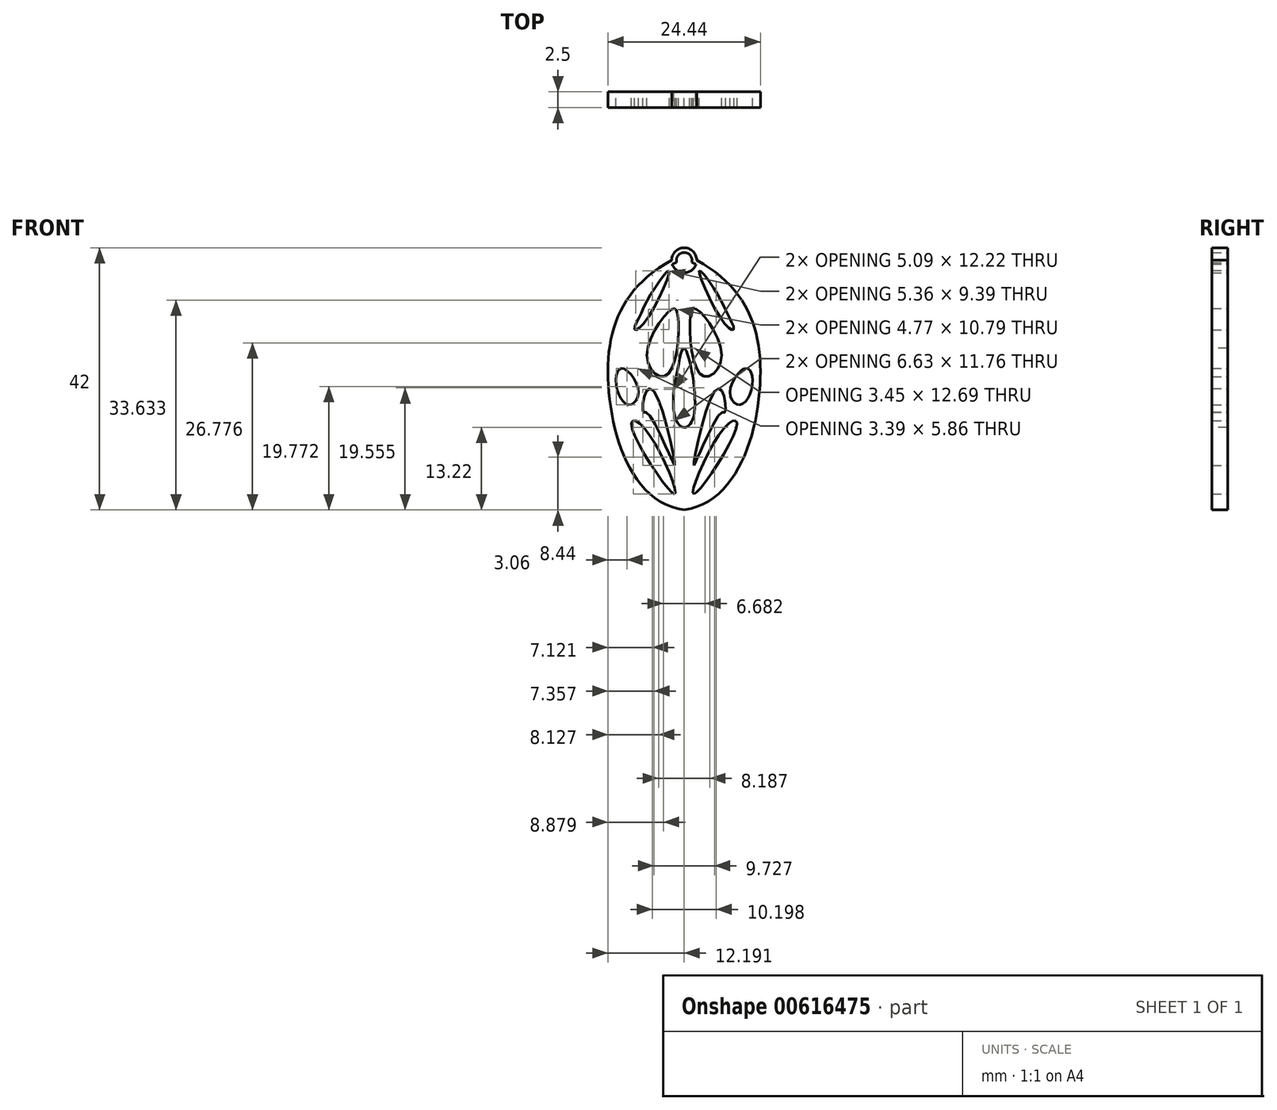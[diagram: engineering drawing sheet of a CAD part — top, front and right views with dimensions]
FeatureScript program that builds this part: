
annotation { "Feature Type Name" : "Feature", "Feature Type Description" : "" }
export const myFeature = defineFeature(function(context is Context, id is Id, definition is map)
    precondition{}
    {
        {
            var Q0;
            Q0=qCreatedBy(makeId("Front.planeOp"),FACE);
            var sketch = newSketch(context, id + "F0", { "sketchPlane" : qUnion([Q0])});
            skCircle(sketch, "E0", {"center": v(0, 20) * mm, "radius": 2 * mm});
            skCircle(sketch, "E1", {"center": v(0, 20) * mm, "radius": 1.25 * mm});
            skFitSpline(sketch, "E2", {"points": [v(2, 20) * mm, v(12.15, 0) * mm, v(0, -20) * mm], "startDerivative": vector(51, -27.77) * mm, "endDerivative": vector(-48.86, -7.06) * mm});
            skLineSegment(sketch, "E3", {"start": v(0, -20) * mm, "end": v(0, -20) * mm});
            skFitSpline(sketch, "E4", {"points": [v(0, 20) * mm, v(12.15, 0) * mm], "startDerivative": vector(21.24, -4.44) * mm, "endDerivative": vector(0.44, -24.75) * mm});
            skLineSegment(sketch, "E5", {"start": v(0, 18.75) * mm, "end": v(0, 18) * mm});
            skFitSpline(sketch, "E6.MirrorCS", {"points": [v(-2, 20) * mm, v(-12.15, 0) * mm, v(0, -20) * mm], "startDerivative": vector(-51, -27.77) * mm, "endDerivative": vector(48.86, -7.06) * mm});
            skFitSpline(sketch, "E7.MirrorCS", {"points": [v(0, 20) * mm, v(-12.15, 0) * mm], "startDerivative": vector(-21.24, -4.44) * mm, "endDerivative": vector(-0.44, -24.75) * mm});
            skFitSpline(sketch, "E8.MirrorCS", {"points": [v(-2, 20) * mm, v(-12.15, 0) * mm, v(0, -20) * mm], "startDerivative": vector(-51, -27.77) * mm, "endDerivative": vector(48.86, -7.06) * mm});
            skPoint(sketch, "E9.orphan", {"position": v(2, 19.9) * mm});
            skPoint(sketch, "E10.orphan", {"position": v(-2, 19.9) * mm});
            skFitSpline(sketch, "E11.MirrorCS", {"points": [v(11.62, 0) * mm, v(8.46, 0) * mm], "startDerivative": vector(-1.65, 0) * mm, "endDerivative": vector(-1.65, 0) * mm});
            skFitSpline(sketch, "E12", {"points": [v(-1.55, -17.44) * mm, v(-8.46, -6.22) * mm, v(-6.8, -6.42) * mm, v(-1.55, -17.44) * mm]});
            skFitSpline(sketch, "E13", {"points": [v(-1.55, -12.89) * mm, v(-2.05, -11.74) * mm, v(-2.21, -11.46) * mm, v(-6.02, -4.37) * mm, v(-6.53, -4.35) * mm, v(-6.05, -0.93) * mm, v(-4.73, -1.2) * mm, v(-1.55, -12.89) * mm]});
            skPoint(sketch, "E14.0.internal.orphan", {"position": v(-1.63, 18.84) * mm});
            skPoint(sketch, "E14.1.internal.orphan", {"position": v(-8.46, 0) * mm});
            skPoint(sketch, "E15.end.orphan", {"position": v(-1.1, 18.33) * mm});
            skPoint(sketch, "E16.MirrorCS.start.orphan", {"position": v(1.1, 18.33) * mm});
            skPoint(sketch, "E17.MirrorCS.start.orphan", {"position": v(1.63, 18.84) * mm});
            skFitSpline(sketch, "E18", {"points": [v(-2.42, 18.33) * mm, v(-5.48, 14.32) * mm, v(-7.05, 11.19) * mm, v(-7.94, 8.97) * mm, v(-6.5, 9.84) * mm, v(-2.42, 18.33) * mm]});
            skFitSpline(sketch, "E19", {"points": [v(-1.96, 12.17) * mm, v(-5.96, 4.3) * mm, v(-2.8, 1.6) * mm, v(-1.1, 11.58) * mm, v(-1.96, 12.17) * mm]});
            skLineSegment(sketch, "E20", {"start": v(0, 18) * mm, "end": v(0, 18) * mm});
            skFitSpline(sketch, "E21.MirrorCS", {"points": [v(0, 20) * mm, v(-12.15, 0) * mm], "startDerivative": vector(-21.24, -4.44) * mm, "endDerivative": vector(-0.44, -24.75) * mm});
            skFitSpline(sketch, "E22.MirrorCS", {"points": [v(0, 20) * mm, v(-12.15, 0) * mm], "startDerivative": vector(-21.24, -4.44) * mm, "endDerivative": vector(-0.44, -24.75) * mm});
            skFitSpline(sketch, "E23.MirrorC", {"points": [v(1.55, -17.44) * mm, v(8.46, -6.22) * mm, v(6.8, -6.42) * mm, v(1.55, -17.44) * mm]});
            skFitSpline(sketch, "E24.MirrorC", {"points": [v(2.42, 18.33) * mm, v(5.48, 14.32) * mm, v(7.05, 11.19) * mm, v(7.94, 8.97) * mm, v(6.5, 9.84) * mm, v(2.42, 18.33) * mm]});
            skFitSpline(sketch, "E25.MirrorCS", {"points": [v(0, 20) * mm, v(-12.15, 0) * mm], "startDerivative": vector(-21.24, -4.44) * mm, "endDerivative": vector(-0.44, -24.75) * mm});
            skFitSpline(sketch, "E26.MirrorC", {"points": [v(1.55, -12.89) * mm, v(2.05, -11.74) * mm, v(2.21, -11.46) * mm, v(6.02, -4.37) * mm, v(6.53, -4.35) * mm, v(6.05, -0.93) * mm, v(4.73, -1.2) * mm, v(1.55, -12.89) * mm]});
            skFitSpline(sketch, "E27.MirrorC", {"points": [v(1.96, 12.17) * mm, v(5.96, 4.3) * mm, v(2.8, 1.6) * mm, v(1.1, 11.58) * mm, v(1.96, 12.17) * mm]});
            skFitSpline(sketch, "E28", {"points": [v(0, 5.9) * mm, v(-0.87, 3.45) * mm, v(-1.62, -0.5) * mm, v(-1.39, -5.33) * mm, v(0, -6.79) * mm, v(1.65, -4.31) * mm, v(0, 5.9) * mm]});
            skLineSegment(sketch, "E29.trimOffspring", {"start": v(0, 5.9) * mm, "end": v(0, -20) * mm});
            skPoint(sketch, "E30.end.orphan", {"position": v(-5.7, 0) * mm});
            skPoint(sketch, "E30.start.orphan", {"position": v(-6.98, 0) * mm});
            skPoint(sketch, "E31.0.internal.orphan", {"position": v(-11.62, 0) * mm});
            skPoint(sketch, "E32.MirrorCS.end.orphan", {"position": v(5.7, 0) * mm});
            skPoint(sketch, "E32.MirrorCS.start.orphan", {"position": v(6.98, 0) * mm});
            skFitSpline(sketch, "E33", {"points": [v(-10.06, 2.7) * mm, v(-10.84, -0.35) * mm, v(-8.81, -3.16) * mm, v(-7.34, -0.9) * mm, v(-10.06, 2.7) * mm]});
            skFitSpline(sketch, "E34.MirrorC", {"points": [v(10.06, 2.7) * mm, v(10.84, -0.35) * mm, v(8.81, -3.16) * mm, v(7.34, -0.9) * mm, v(10.06, 2.7) * mm]});
            skSolve(sketch);
        }
        {
            var Q0;
            Q0=qSketchRegion(id+"F0",true);
            extrude(context, id + "F1", {"entities" : qUnion([Q0]), "depth" : 2.5 * mm, "offsetDistance" : 25 * mm});
        }
    });
